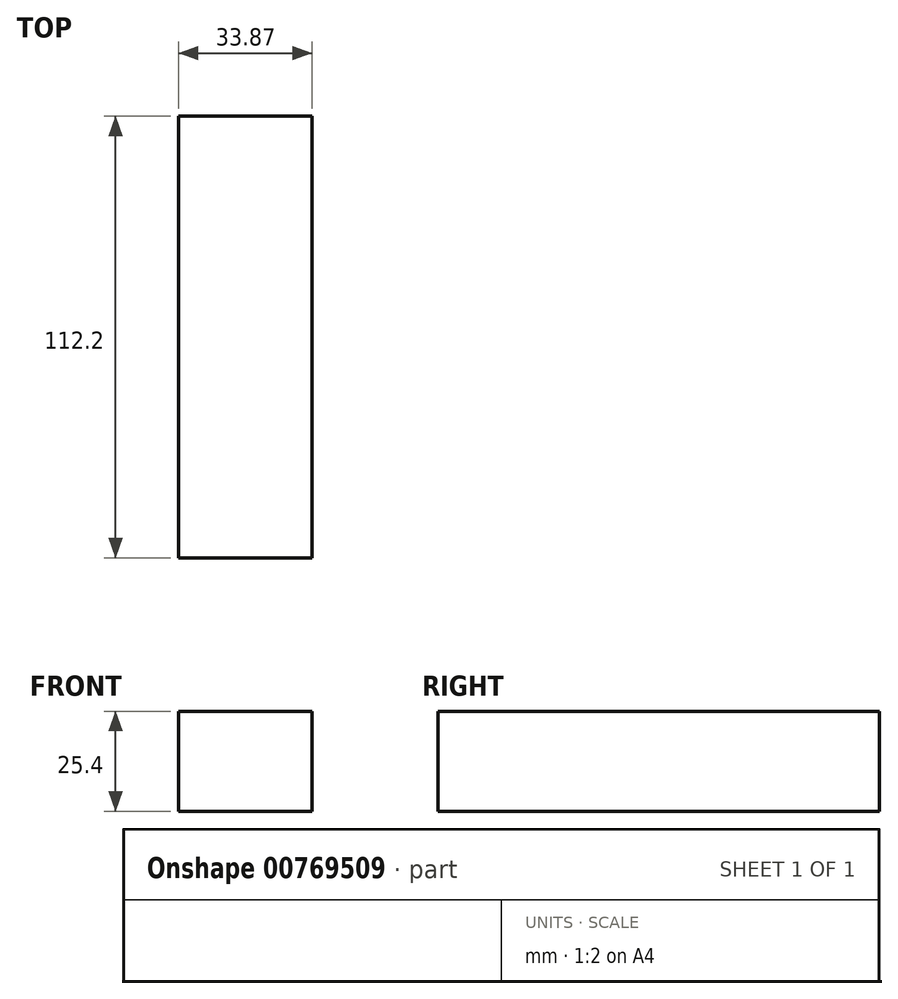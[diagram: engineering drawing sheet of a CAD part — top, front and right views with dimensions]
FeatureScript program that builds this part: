
annotation { "Feature Type Name" : "Feature", "Feature Type Description" : "" }
export const myFeature = defineFeature(function(context is Context, id is Id, definition is map)
    precondition{}
    {
        {
            var Q0;
            Q0=qCreatedBy(makeId("Top.planeOp"),FACE);
            var sketch = newSketch(context, id + "F0", { "sketchPlane" : qUnion([Q0])});
            skLineSegment(sketch, "E0.bottom", {"start": v(-61.36, 56.08) * mm, "end": v(-27.49, 56.08) * mm});
            skLineSegment(sketch, "E0.top", {"start": v(-61.36, -56.12) * mm, "end": v(-27.49, -56.12) * mm});
            skLineSegment(sketch, "E0.left", {"start": v(-61.36, 56.08) * mm, "end": v(-61.36, -56.12) * mm});
            skLineSegment(sketch, "E0.right", {"start": v(-27.49, 56.08) * mm, "end": v(-27.49, -56.12) * mm});
            skSolve(sketch);
        }
        {
            var Q0;
            Q0=makeQuery(id+"F0.imprint","IMPRINT",FACE,{"disambiguationData":[TD([[makeQuery(id+"F0.imprint","IMPRINT",EDGE,{"derivedFrom":sQuery(id+"F0.wireOp",EDGE,"E0.bottom")}),-1.0]])]});
            extrude(context, id + "F1", {"entities" : qUnion([Q0]), "depth" : 25.4 * mm, "offsetDistance" : 25.4 * mm});
        }
    });
